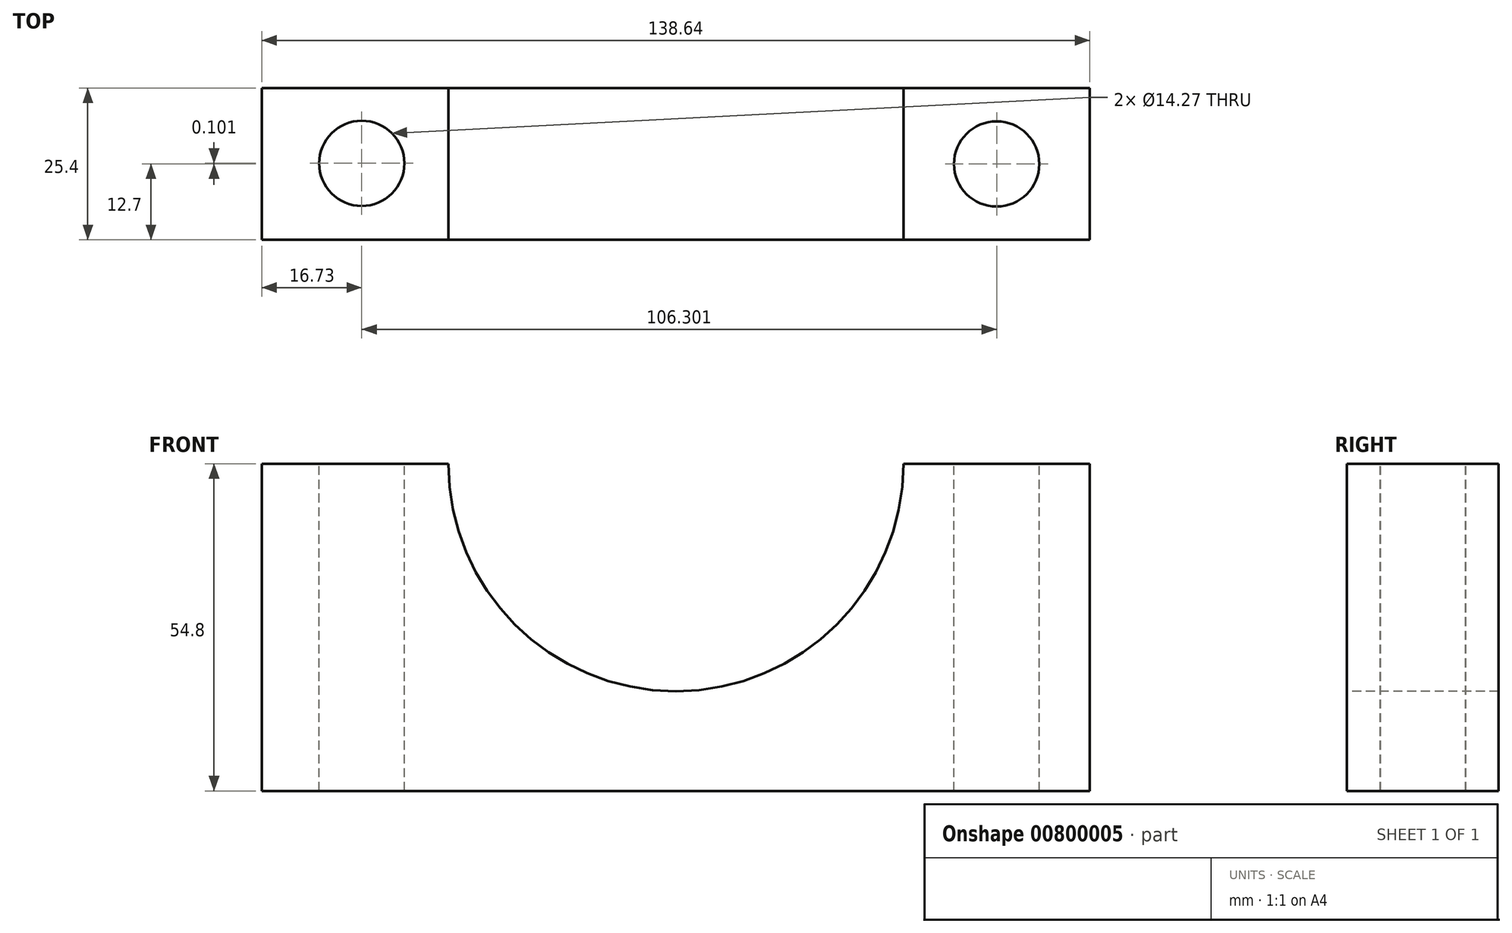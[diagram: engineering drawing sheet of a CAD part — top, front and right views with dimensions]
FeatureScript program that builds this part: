
annotation { "Feature Type Name" : "Feature", "Feature Type Description" : "" }
export const myFeature = defineFeature(function(context is Context, id is Id, definition is map)
    precondition{}
    {
        {
            var Q0;
            Q0=qCreatedBy(makeId("Front.planeOp"),FACE);
            var sketch = newSketch(context, id + "F0", { "sketchPlane" : qUnion([Q0])});
            skLineSegment(sketch, "E0.bottom", {"start": v(69.32, 0) * mm, "end": v(-69.32, 0) * mm});
            skLineSegment(sketch, "E0.top", {"start": v(69.32, -54.8) * mm, "end": v(-69.32, -54.8) * mm});
            skLineSegment(sketch, "E0.left", {"start": v(69.32, 0) * mm, "end": v(69.32, -54.8) * mm});
            skLineSegment(sketch, "E0.right", {"start": v(-69.32, 0) * mm, "end": v(-69.32, -54.8) * mm});
            skPoint(sketch, "E0.middle", {"position": v(0, -27.4) * mm});
            skSolve(sketch);
        }
        {
            var Q0;
            Q0 = qSketchRegion(id + "F0", true);
            extrude(context, id + "F1", {"entities" : qUnion([Q0]), "depth" : 25.4 * mm, "offsetDistance" : 25.4 * mm});
        }
        {
            var Q0;
            Q0=makeQuery(id+"F1.opExtrude","CAP_FACE",FACE,{"disambiguationData":[OSD([sQuery(id+"F0.wireOp",EDGE,"E0.bottom"),sQuery(id+"F0.wireOp",EDGE,"E0.top"),sQuery(id+"F0.wireOp",EDGE,"E0.left"),sQuery(id+"F0.wireOp",EDGE,"E0.right")])],"isStart":false});
            var sketch = newSketch(context, id + "F2", { "sketchPlane" : qUnion([Q0])});
            skPoint(sketch, "E1", {"position": v(0, 0) * mm});
            skPoint(sketch, "E2", {"position": v(22.09, -24.32) * mm});
            skPoint(sketch, "E3", {"position": v(-0.18, -55.35) * mm});
            skPoint(sketch, "E4", {"position": v(0, 116.3) * mm});
            skSolve(sketch);
        }
        {
            var Q0;
            Q0=sQuery(id+"F2.wireOp",VERTEX,"E1");
            var Q1;
            Q1=makeQuery(id+"F1.opExtrude","SWEPT_BODY",BODY,{"disambiguationData":[OSD([sQuery(id+"F0.wireOp",EDGE,"E0.bottom"),sQuery(id+"F0.wireOp",EDGE,"E0.top"),sQuery(id+"F0.wireOp",EDGE,"E0.left"),sQuery(id+"F0.wireOp",EDGE,"E0.right")])]});
            hole(context, id + "F3", {"style" : HoleStyle.SIMPLE, "endStyle" : HoleEndStyle.THROUGH, "holeDiameter" : 76.2 * mm, "majorDiameter" : 6.35 * mm, "isTappedThrough" : true, "tappedDepth" : 12.7 * mm, "tapClearance" : 3, "locations" : qUnion([Q0]), "scope" : qUnion([Q1])});
        }
        {
            var Q0;
            {var subQ1=sQuery(id+"F0.wireOp",EDGE,"E0.left");var subQ3=sQuery(id+"F0.wireOp",EDGE,"E0.bottom");Q0=makeQuery(id+"F3.hole-0.boolean.opBoolean","SPLIT",FACE,{"disambiguationData":[TD([makeQuery(id+"F1.opExtrude","SWEPT_FACE",FACE,{"disambiguationData":[OSD([subQ1])]})])],"derivedFrom":makeQuery(id+"F1.opExtrude","SWEPT_FACE",FACE,{"disambiguationData":[OSD([subQ3])]})});}
            var sketch = newSketch(context, id + "F4", { "sketchPlane" : qUnion([Q0])});
            skLineSegment(sketch, "E5", {"start": v(53.71, 0) * mm, "end": v(53.71, 0) * mm});
            skLineSegment(sketch, "E6", {"start": v(53.71, 0) * mm, "end": v(53.71, -25.4) * mm});
            skLineSegment(sketch, "E7", {"start": v(-52.59, 0) * mm, "end": v(-52.59, -25.2) * mm});
            skPoint(sketch, "E8", {"position": v(-52.59, -25.2) * mm});
            skPoint(sketch, "E9", {"position": v(53.71, -12.7) * mm});
            skPoint(sketch, "E10", {"position": v(-52.59, -12.6) * mm});
            skSolve(sketch);
        }
        {
            var Q0;
            Q0=sQuery(id+"F4.wireOp",VERTEX,"E9");
            var Q1;
            Q1=sQuery(id+"F4.wireOp",VERTEX,"E10");
            var Q2;
            Q2=makeQuery(id+"F1.opExtrude","SWEPT_BODY",BODY,{"disambiguationData":[OSD([sQuery(id+"F0.wireOp",EDGE,"E0.bottom"),sQuery(id+"F0.wireOp",EDGE,"E0.top"),sQuery(id+"F0.wireOp",EDGE,"E0.left"),sQuery(id+"F0.wireOp",EDGE,"E0.right")])]});
            hole(context, id + "F5", {"style" : HoleStyle.SIMPLE, "endStyle" : HoleEndStyle.THROUGH, "holeDiameter" : 14.27 * mm, "majorDiameter" : 6.35 * mm, "isTappedThrough" : true, "tappedDepth" : 12.7 * mm, "tapClearance" : 3, "locations" : qUnion([Q0, Q1]), "scope" : qUnion([Q2])});
        }
    });
